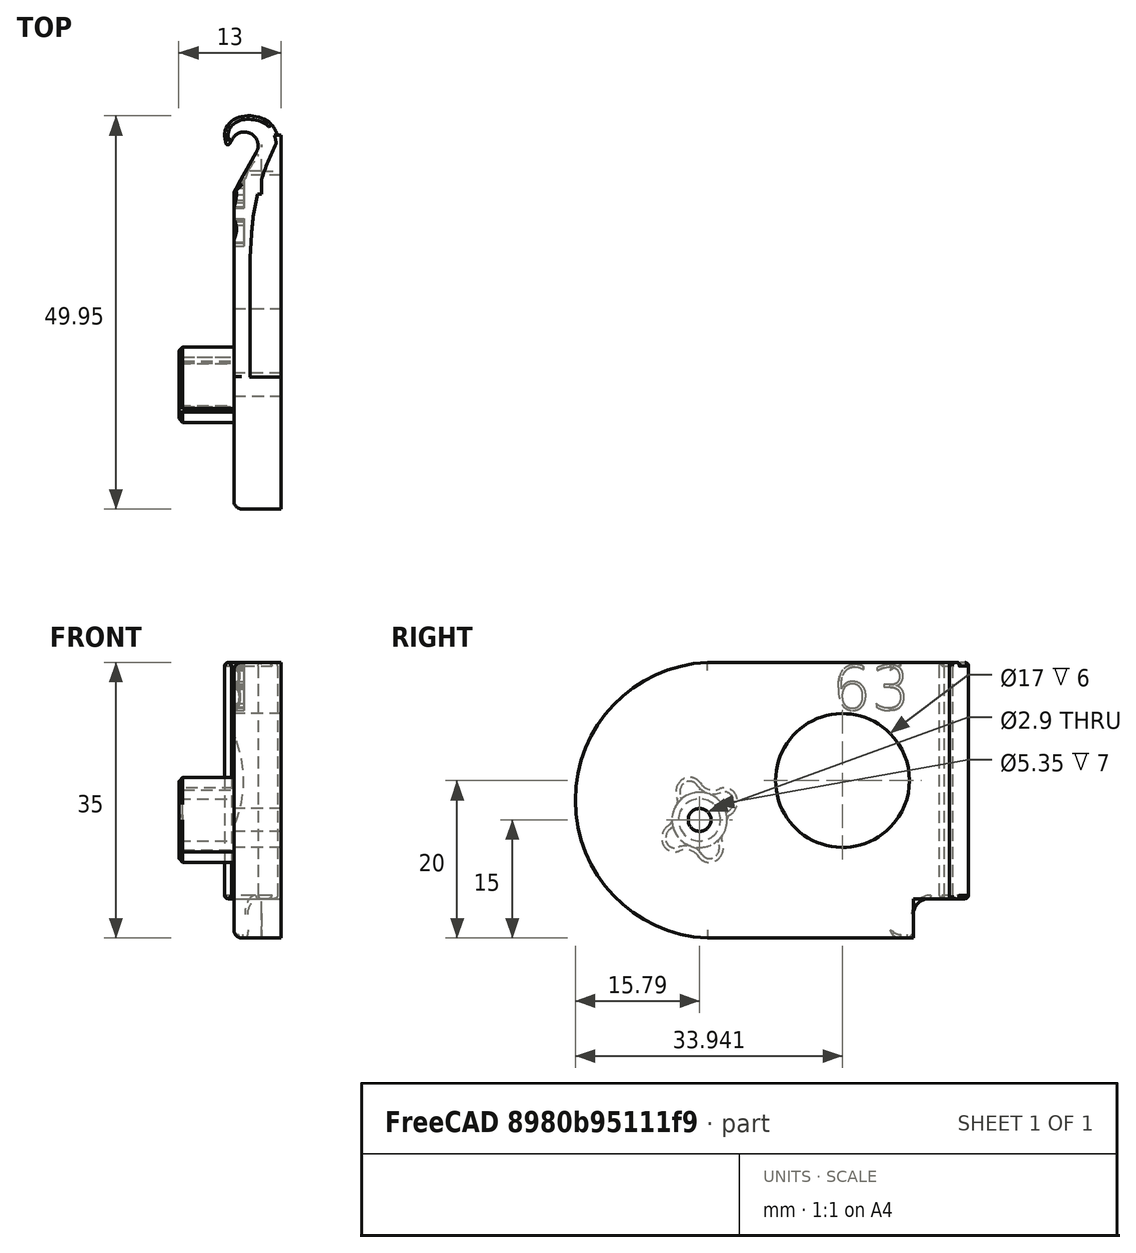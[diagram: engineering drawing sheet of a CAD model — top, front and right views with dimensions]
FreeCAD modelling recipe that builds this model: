
FCSTD DOCUMENT  (FreeCAD 0.18R)
Label: hinge-right-163deg-flat
License: All rights reserved
LicenseURL: http://en.wikipedia.org/wiki/All_rights_reserved
objects: App::FeaturePython×6, Part::FeaturePython×2, Part::Part2DObjectPython×1, Part::Extrusion×1, Part::Cut×1
note: 5 computed .brp shape members not serialized (recipe doc carries the construction recipe); baked Part::Feature solids carry a one-line shape summary decoded from their .brp

FEATURE [Part::FeaturePython] pillar_base_001  label="pillar-base_001"  # a2plus imported part (geometry in sourceFile) (typed FeaturePython)
  Placement = pos=(0.000608724,-57.7305,22.1549) rot=(-1,0,0;0.732864rad)
  a2p_Version = V0.1
  fixedPosition = false
  objectType = a2pPart
  sourceFile = ./parts/pillar-base.fcstd
  subassemblyImport = false
  timeLastImport = 1.60452e+09
  updateColors = true
FEATURE [Part::Part2DObjectPython] ShapeString  # Draft 2D object (typed FeaturePython)
  FontFile = <path>
  Placement = pos=(1.61,10.5,29) rot=(0.57735,-0.57735,-0.57735;2.0944rad)
  Size = 6
  String = 63
  Tracking = 0
FEATURE [Part::Extrusion] Extrude
  Base = -> ShapeString
  Dir = (-1,0,0)
  DirMode = 2
  FaceMakerClass = Part::FaceMakerBullseye
  LengthFwd = 3.5
  LengthRev = 0
  Placement = pos=(0,0,0) rot=(0,0,1;3.14159rad)
  Solid = false
  Symmetric = false
FEATURE [Part::FeaturePython] bracket_right_flat_001  label="bracket-right-flat_001"  # a2plus imported part (geometry in sourceFile) (typed FeaturePython)
  Placement = pos=(0,0,0) rot=(0,0,1;3.14159rad)
  a2p_Version = V0.1
  fixedPosition = true
  objectType = a2pPart
  sourceFile = ./parts/bracket-right-flat.fcstd
  subassemblyImport = false
  timeLastImport = 1.60489e+09
  updateColors = true
FEATURE [App::FeaturePython] axisCoincident_001  label="axisCoincident_001__bracket-right-flat_001"  # a2plus constraint (typed FeaturePython)
  Object1 = pillar_base_001
  Object2 = bracket_right_flat_001
  ParentTreeObject = -> pillar_base_001
  SubElement1 = Face17
  SubElement2 = Face31
  Suppressed = false
  Type = axial
  directionConstraint = 1
  lockRotation = false
FEATURE [App::FeaturePython] axisCoincident_001_mirror  label="axisCoincident_001__pillar-base_001"  # a2plus constraint (typed FeaturePython)
  Object1 = pillar_base_001
  Object2 = bracket_right_flat_001
  ParentTreeObject = -> bracket_right_flat_001
  SubElement1 = Face17
  SubElement2 = Face31
  Suppressed = false
  Type = axial
  directionConstraint = 1
  lockRotation = false
FEATURE [App::FeaturePython] planeCoincident_001  label="planeCoincident_001__bracket-right-flat_001"  # a2plus constraint (typed FeaturePython)
  Object1 = pillar_base_001
  Object2 = bracket_right_flat_001
  ParentTreeObject = -> pillar_base_001
  SubElement1 = Face1
  SubElement2 = Face57
  Suppressed = false
  Type = plane
  directionConstraint = 1
  offset = 0
FEATURE [App::FeaturePython] planeCoincident_001_mirror  label="planeCoincident_001__pillar-base_001"  # a2plus constraint (typed FeaturePython)
  Object1 = pillar_base_001
  Object2 = bracket_right_flat_001
  ParentTreeObject = -> bracket_right_flat_001
  SubElement1 = Face1
  SubElement2 = Face57
  Suppressed = false
  Type = plane
  directionConstraint = 1
  offset = 0
FEATURE [Part::Cut] Cut
  Base = -> bracket_right_flat_001
  Tool = -> Extrude
FEATURE [App::FeaturePython] axisCoincident_001_mirror001  label="axisCoincident_001__bracket-right-flat_001_"  # a2plus constraint (typed FeaturePython)
  Object1 = pillar_base_001
  Object2 = bracket_right_flat_001
  ParentTreeObject = -> pillar_base_001
  SubElement1 = Face17
  SubElement2 = Face31
  Suppressed = false
  Type = axial
  directionConstraint = 1
  lockRotation = false
FEATURE [App::FeaturePython] planeCoincident_001_mirror001  label="planeCoincident_001__bracket-right-flat_001_"  # a2plus constraint (typed FeaturePython)
  Object1 = pillar_base_001
  Object2 = bracket_right_flat_001
  ParentTreeObject = -> pillar_base_001
  SubElement1 = Face1
  SubElement2 = Face57
  Suppressed = false
  Type = plane
  directionConstraint = 1
  offset = 0
note: 1 file-system path scrubbed to <path> (originals preserved in the JSON sidecar)
